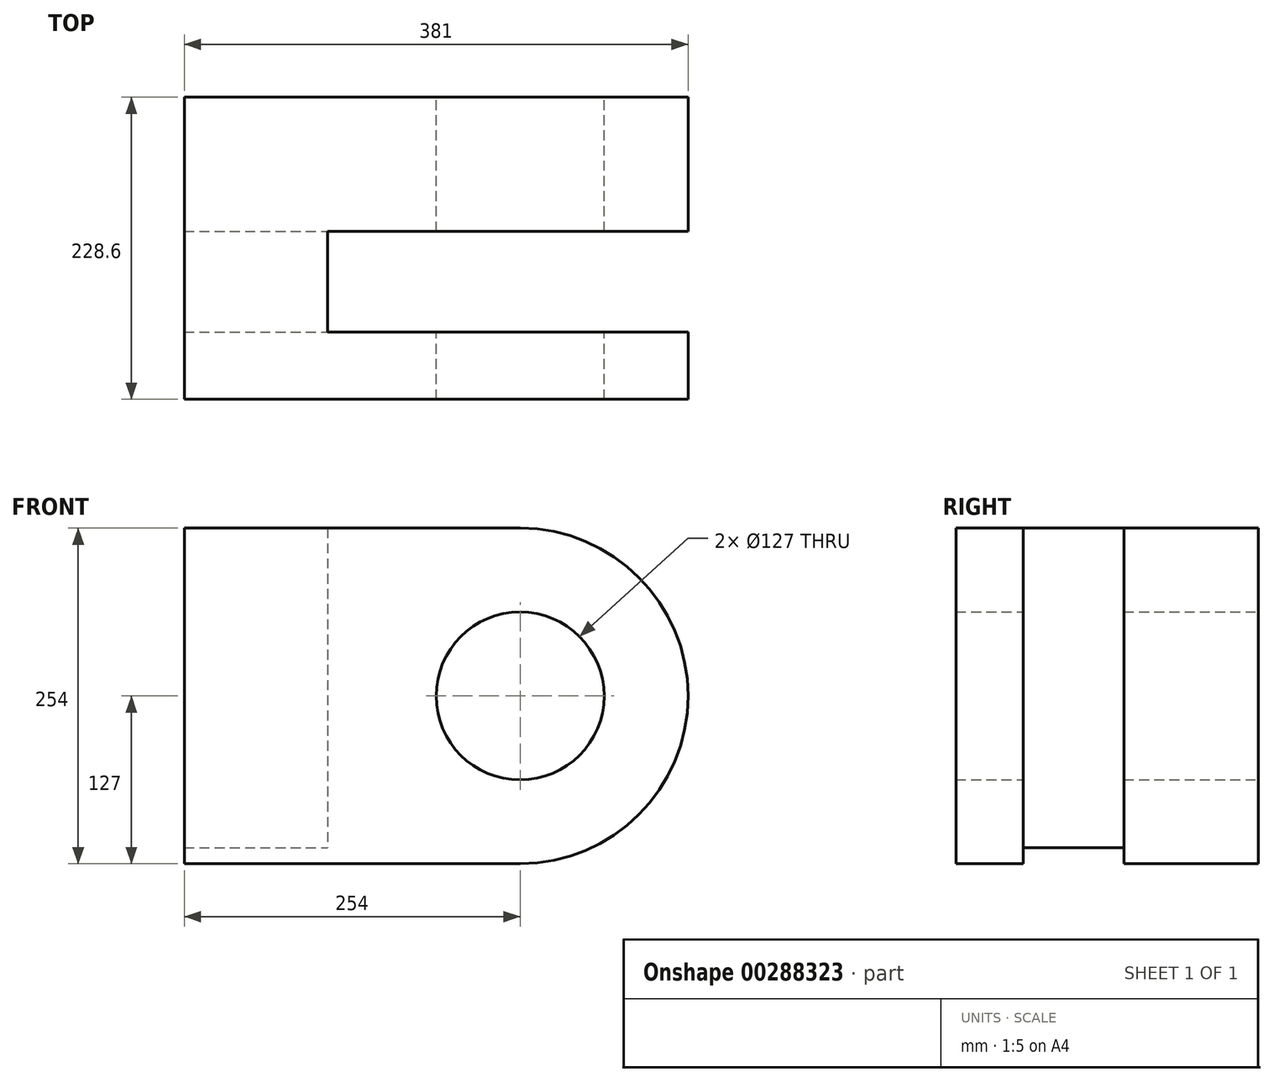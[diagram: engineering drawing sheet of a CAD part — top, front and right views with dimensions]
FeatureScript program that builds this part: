
annotation { "Feature Type Name" : "Feature", "Feature Type Description" : "" }
export const myFeature = defineFeature(function(context is Context, id is Id, definition is map)
    precondition{}
    {
        {
            var Q0;
            Q0=qCreatedBy(makeId("Front.planeOp"),FACE);
            var sketch = newSketch(context, id + "F0", { "sketchPlane" : qUnion([Q0])});
            skCircle(sketch, "E0", {"center": v(0, 0) * mm, "radius": 63.5 * mm});
            skArc(sketch, "E1", {"start": v(0, -127) * mm, "mid": v(127, 0) * mm, "end": v(0, 127) * mm});
            skLineSegment(sketch, "E2", {"start": v(0, 127) * mm, "end": v(-254, 127) * mm});
            skLineSegment(sketch, "E3", {"start": v(-254, 127) * mm, "end": v(-254, -127) * mm});
            skLineSegment(sketch, "E4", {"start": v(-254, -127) * mm, "end": v(0, -127) * mm});
            skSolve(sketch);
        }
        {
            var Q0;
            Q0=makeQuery(id+"F0.imprint","IMPRINT",FACE,{"disambiguationData":[TD([[makeQuery(id+"F0.imprint","IMPRINT",EDGE,{"derivedFrom":sQuery(id+"F0.wireOp",EDGE,"E0")}),-1.0]])]});
            extrude(context, id + "F1", {"entities" : qUnion([Q0]), "depth" : 101.6 * mm});
        }
        {
            var Q0;
            Q0=makeQuery(id+"F1.opExtrude","CAP_FACE",FACE,{"disambiguationData":[OSD([sQuery(id+"F0.wireOp",EDGE,"E0"),sQuery(id+"F0.wireOp",EDGE,"E1"),sQuery(id+"F0.wireOp",EDGE,"E2"),sQuery(id+"F0.wireOp",EDGE,"E3"),sQuery(id+"F0.wireOp",EDGE,"E4")])],"isStart":false});
            cPlane(context, id + "F2", {"entities" : qUnion([Q0]), "cplaneType" : CPlaneType.OFFSET, "offset" : 76.2 * mm, "width" : 152.4 * mm, "height" : 152.4 * mm});
        }
        {
            var Q0;
            Q0=qCreatedBy(id+"F2.planeOp",FACE);
            var sketch = newSketch(context, id + "F3", { "sketchPlane" : qUnion([Q0])});
            skLineSegment(sketch, "E5.0.0", {"start": v(-254, 127) * mm, "end": v(-254, -127) * mm});
            skLineSegment(sketch, "E5.0.1", {"start": v(-254, -127) * mm, "end": v(0, -127) * mm});
            skArc(sketch, "E5.0.2", {"start": v(0, -127) * mm, "mid": v(127, 0) * mm, "end": v(0, 127) * mm});
            skLineSegment(sketch, "E5.0.3", {"start": v(0, 127) * mm, "end": v(-254, 127) * mm});
            skCircle(sketch, "E6.0", {"center": v(0, 0) * mm, "radius": 63.5 * mm});
            skSolve(sketch);
        }
        {
            var Q0;
            Q0=makeQuery(id+"F3.imprint","IMPRINT",FACE,{"disambiguationData":[TD([[makeQuery(id+"F3.imprint","IMPRINT",EDGE,{"derivedFrom":sQuery(id+"F3.wireOp",EDGE,"E5.0.0")}),1.0]])]});
            extrude(context, id + "F4", {"entities" : qUnion([Q0]), "depth" : 50.8 * mm});
        }
        {
            var Q0;
            Q0=makeQuery(id+"F1.opExtrude","CAP_FACE",FACE,{"disambiguationData":[OSD([sQuery(id+"F0.wireOp",EDGE,"E0"),sQuery(id+"F0.wireOp",EDGE,"E1"),sQuery(id+"F0.wireOp",EDGE,"E2"),sQuery(id+"F0.wireOp",EDGE,"E3"),sQuery(id+"F0.wireOp",EDGE,"E4")])],"isStart":false});
            var sketch = newSketch(context, id + "F5", { "sketchPlane" : qUnion([Q0])});
            skLineSegment(sketch, "E7.bottom", {"start": v(-254, 127) * mm, "end": v(-145.64, 127) * mm});
            skLineSegment(sketch, "E7.top", {"start": v(-254, -114.9) * mm, "end": v(-145.64, -114.9) * mm});
            skLineSegment(sketch, "E7.left", {"start": v(-254, 127) * mm, "end": v(-254, -114.9) * mm});
            skLineSegment(sketch, "E7.right", {"start": v(-145.64, 127) * mm, "end": v(-145.64, -114.9) * mm});
            skSolve(sketch);
        }
        {
            var Q0;
            Q0=makeQuery(id+"F5.imprint","IMPRINT",FACE,{"disambiguationData":[TD([[makeQuery(id+"F5.imprint","IMPRINT",EDGE,{"derivedFrom":sQuery(id+"F5.wireOp",EDGE,"E7.bottom")}),1.0]])]});
            extrude(context, id + "F6", {"entities" : qUnion([Q0]), "operationType" : NewBodyOperationType.ADD, "endBound" : BoundingType.UP_TO_NEXT, "depth" : 25.4 * mm});
        }
    });
